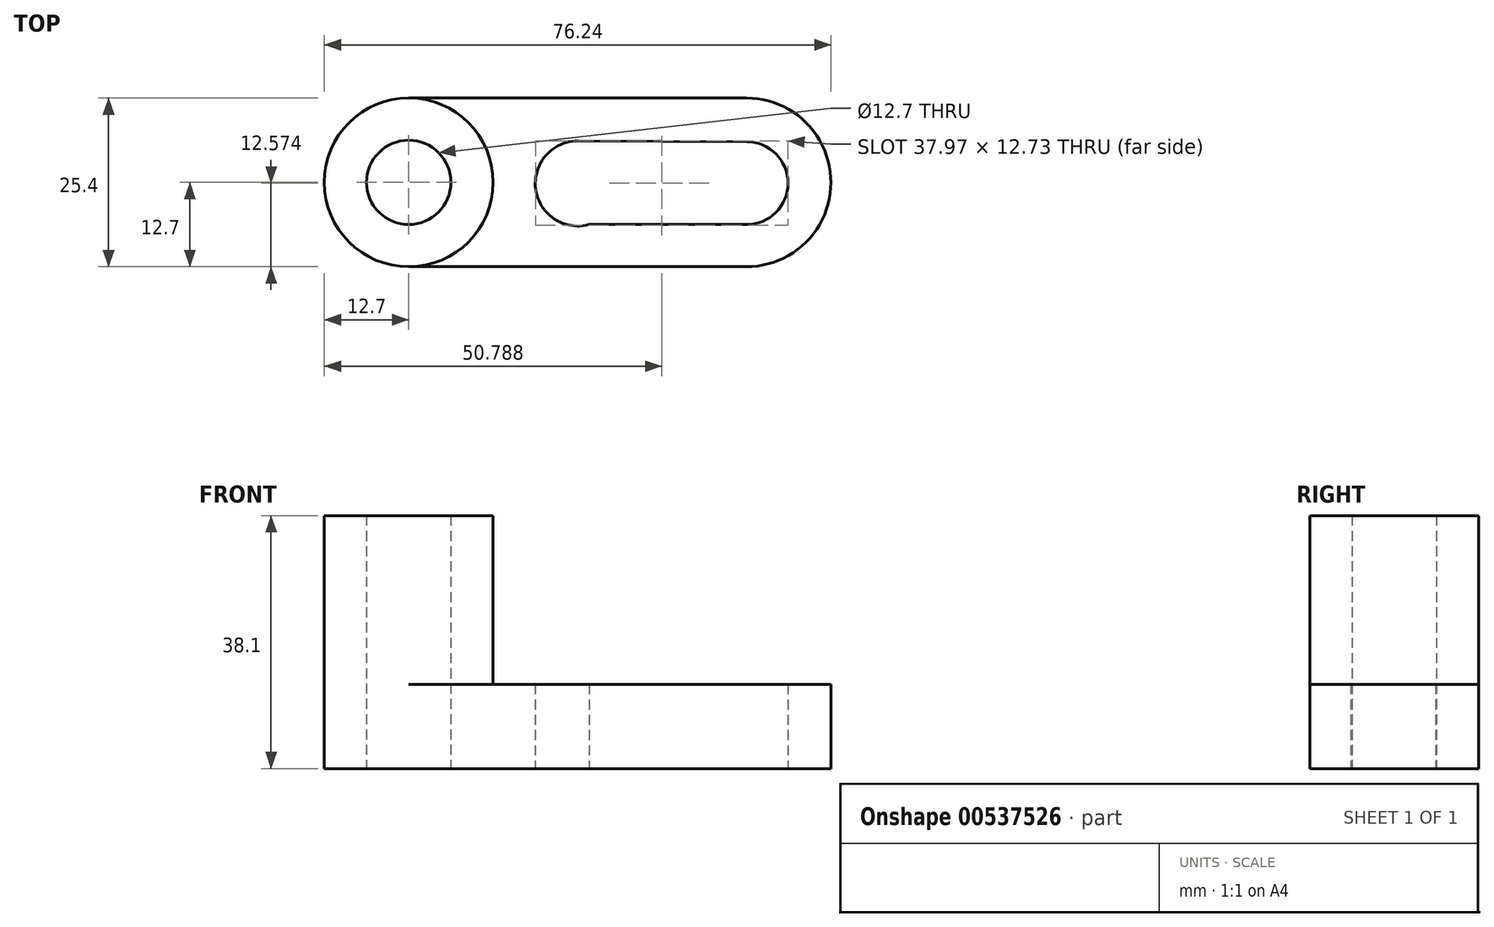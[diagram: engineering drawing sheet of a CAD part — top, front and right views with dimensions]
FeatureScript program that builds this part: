
annotation { "Feature Type Name" : "Feature", "Feature Type Description" : "" }
export const myFeature = defineFeature(function(context is Context, id is Id, definition is map)
    precondition{}
    {
        {
            var Q0;
            Q0=qCreatedBy(makeId("Top.planeOp"),FACE);
            var sketch = newSketch(context, id + "F0", { "sketchPlane" : qUnion([Q0])});
            skLineSegment(sketch, "E0", {"start": v(0, 0) * mm, "end": v(50.8, 0) * mm});
            skLineSegment(sketch, "E1", {"start": v(50.84, 25.4) * mm, "end": v(0, 25.4) * mm});
            skArc(sketch, "E2", {"start": v(50.8, 0) * mm, "mid": v(63.54, 12.68) * mm, "end": v(50.84, 25.4) * mm});
            skArc(sketch, "E3", {"start": v(0, 25.4) * mm, "mid": v(-12.7, 12.7) * mm, "end": v(0, 0) * mm});
            skCircle(sketch, "E4", {"center": v(0, 12.7) * mm, "radius": 6.35 * mm});
            skLineSegment(sketch, "E5", {"start": v(50.88, 18.83) * mm, "end": v(25.48, 18.94) * mm});
            skLineSegment(sketch, "E6", {"start": v(27.13, 6.35) * mm, "end": v(50.84, 6.35) * mm});
            skArc(sketch, "E7", {"start": v(50.84, 6.35) * mm, "mid": v(57.07, 12.56) * mm, "end": v(50.88, 18.83) * mm});
            skArc(sketch, "E8", {"start": v(25.48, 18.94) * mm, "mid": v(19.1, 11.7) * mm, "end": v(27.13, 6.35) * mm});
            skSolve(sketch);
        }
        {
            var Q0;
            Q0 = qSketchRegion(id + "F0", true);
            extrude(context, id + "F1", {"entities" : qUnion([Q0]), "depth" : 38.1 * mm, "offsetDistance" : 25.4 * mm});
        }
        {
            var Q0;
            Q0=makeQuery(id+"F1.opExtrude","CAP_FACE",FACE,{"disambiguationData":[OSD([sQuery(id+"F0.wireOp",EDGE,"E0"),sQuery(id+"F0.wireOp",EDGE,"E1"),sQuery(id+"F0.wireOp",EDGE,"E2"),sQuery(id+"F0.wireOp",EDGE,"E3"),sQuery(id+"F0.wireOp",EDGE,"E4"),sQuery(id+"F0.wireOp",EDGE,"E5"),sQuery(id+"F0.wireOp",EDGE,"E6"),sQuery(id+"F0.wireOp",EDGE,"E7"),sQuery(id+"F0.wireOp",EDGE,"E8")])],"isStart":false});
            var sketch = newSketch(context, id + "F2", { "sketchPlane" : qUnion([Q0])});
            skArc(sketch, "E9", {"start": v(0, 0) * mm, "mid": v(12.7, 12.7) * mm, "end": v(0, 25.4) * mm});
            skSolve(sketch);
        }
        {
            var Q0;
            Q0=makeQuery(id+"F2.imprint","IMPRINT",FACE,{"disambiguationData":[TD([[makeQuery(id+"F2.imprint","IMPRINT",EDGE,{"derivedFrom":sQuery(id+"F2.wireOp",EDGE,"E9")}),-1.0]])]});
            extrude(context, id + "F3", {"entities" : qUnion([Q0]), "operationType" : NewBodyOperationType.REMOVE, "oppositeDirection" : true, "depth" : 25.4 * mm, "offsetDistance" : 25.4 * mm});
        }
    });
